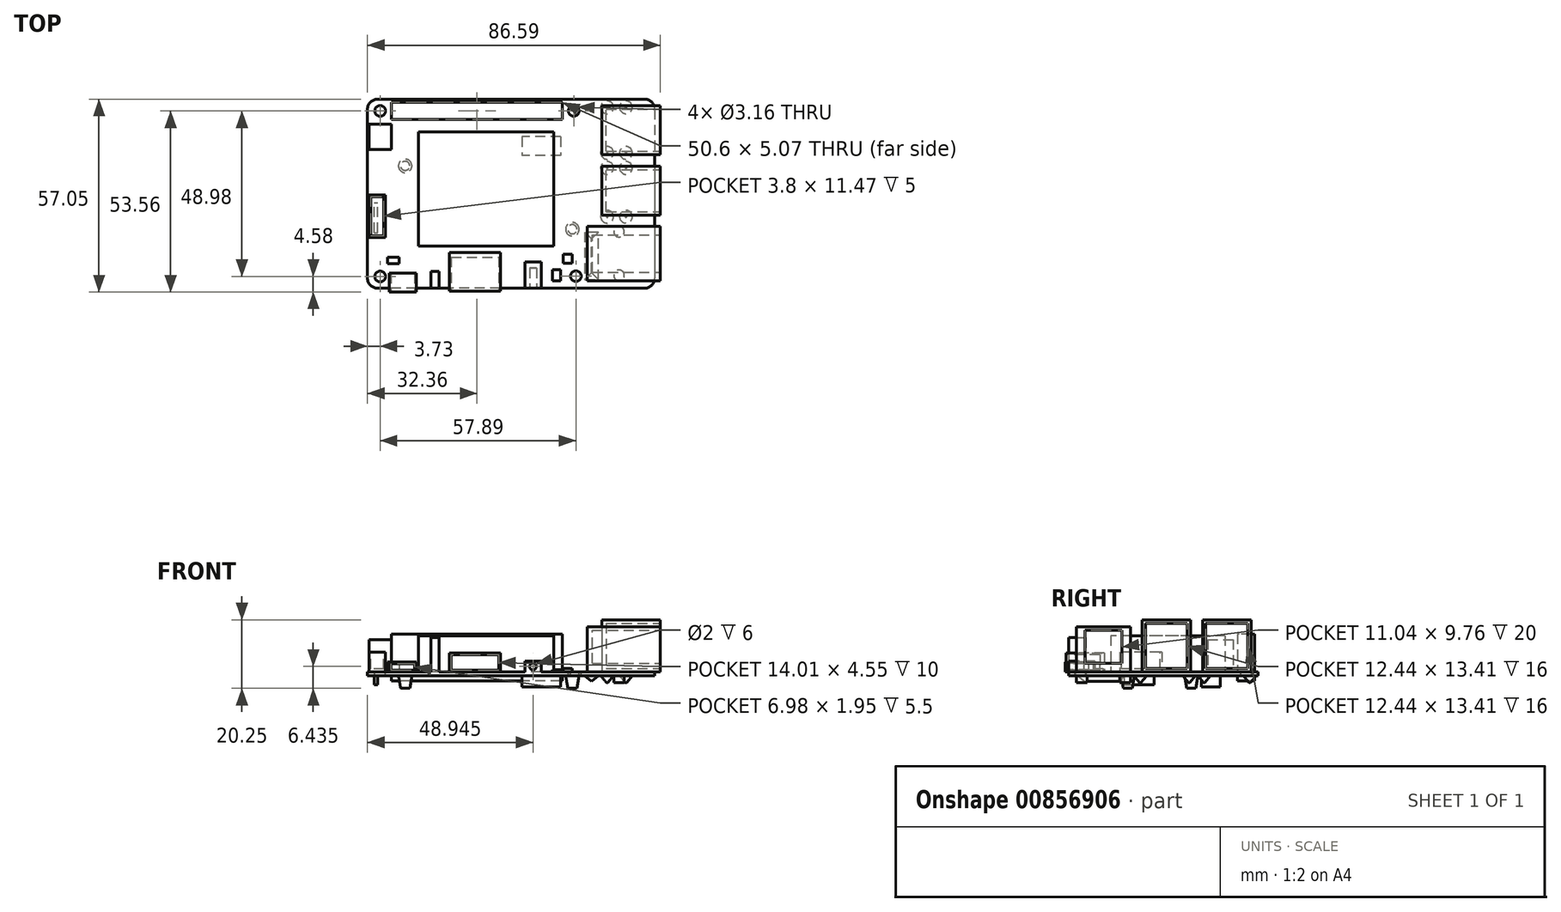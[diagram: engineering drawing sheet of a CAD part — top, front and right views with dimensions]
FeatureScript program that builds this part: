
annotation { "Feature Type Name" : "Feature", "Feature Type Description" : "" }
export const myFeature = defineFeature(function(context is Context, id is Id, definition is map)
    precondition{}
    {
        {
            var Q0;
            Q0=qCreatedBy(makeId("Top.planeOp"),FACE);
            var sketch = newSketch(context, id + "F0", { "sketchPlane" : qUnion([Q0])});
            skLineSegment(sketch, "E0.bottom", {"start": v(42.46, 27.98) * mm, "end": v(-42.46, 27.98) * mm});
            skLineSegment(sketch, "E0.top", {"start": v(42.46, -27.98) * mm, "end": v(-42.46, -27.98) * mm});
            skLineSegment(sketch, "E0.left", {"start": v(42.46, 27.98) * mm, "end": v(42.46, -27.98) * mm});
            skLineSegment(sketch, "E0.right", {"start": v(-42.46, 27.98) * mm, "end": v(-42.46, -27.98) * mm});
            skPoint(sketch, "E0.middle", {"position": v(0, 0) * mm});
            skSolve(sketch);
        }
        {
            var Q0;
            Q0=qSketchRegion(id+"F0",true);
            extrude(context, id + "F1", {"entities" : qUnion([Q0]), "depth" : 1.15 * mm, "offsetDistance" : 25 * mm});
        }
        {
            var Q0;
            Q0=makeQuery(id+"F1.opExtrude","CAP_FACE",FACE,{"disambiguationData":[OSD([sQuery(id+"F0.wireOp",EDGE,"E0.bottom"),sQuery(id+"F0.wireOp",EDGE,"E0.top"),sQuery(id+"F0.wireOp",EDGE,"E0.left"),sQuery(id+"F0.wireOp",EDGE,"E0.right")])],"isStart":false});
            var sketch = newSketch(context, id + "F2", { "sketchPlane" : qUnion([Q0])});
            skLineSegment(sketch, "E1.top", {"start": v(44.05, -9.69) * mm, "end": v(22.48, -9.69) * mm});
            skLineSegment(sketch, "E1.left", {"start": v(44.05, -25.73) * mm, "end": v(44.05, -9.69) * mm});
            skLineSegment(sketch, "E1.right", {"start": v(22.48, -25.73) * mm, "end": v(22.48, -9.69) * mm});
            skLineSegment(sketch, "E2", {"start": v(44.05, -25.73) * mm, "end": v(22.48, -25.73) * mm});
            skSolve(sketch);
        }
        {
            var Q0;
            Q0=qSketchRegion(id+"F2",true);
            extrude(context, id + "F3", {"entities" : qUnion([Q0]), "operationType" : NewBodyOperationType.ADD, "depth" : 13.33 * mm, "offsetDistance" : 25 * mm});
        }
        {
            var Q0;
            Q0=makeQuery(id+"F3.opExtrude","SWEPT_FACE",FACE,{"disambiguationData":[OSD([sQuery(id+"F2.wireOp",EDGE,"E1.left")])]});
            var sketch = newSketch(context, id + "F4", { "sketchPlane" : qUnion([Q0])});
            skLineSegment(sketch, "E3", {"start": v(-23.23, 13.45) * mm, "end": v(-12.19, 13.45) * mm});
            skLineSegment(sketch, "E4", {"start": v(-23.23, 3.7) * mm, "end": v(-23.23, 13.45) * mm});
            skLineSegment(sketch, "E5", {"start": v(-23.23, 3.7) * mm, "end": v(-12.19, 3.7) * mm});
            skLineSegment(sketch, "E6", {"start": v(-12.19, 3.7) * mm, "end": v(-12.19, 13.45) * mm});
            skSolve(sketch);
        }
        {
            var Q0;
            Q0=qSketchRegion(id+"F4",true);
            extrude(context, id + "F5", {"entities" : qUnion([Q0]), "operationType" : NewBodyOperationType.REMOVE, "oppositeDirection" : true, "depth" : 20 * mm, "offsetDistance" : 25 * mm});
        }
        {
            var Q0;
            Q0=makeQuery(id+"F1.opExtrude","CAP_FACE",FACE,{"disambiguationData":[OSD([sQuery(id+"F0.wireOp",EDGE,"E0.bottom"),sQuery(id+"F0.wireOp",EDGE,"E0.top"),sQuery(id+"F0.wireOp",EDGE,"E0.left"),sQuery(id+"F0.wireOp",EDGE,"E0.right")])],"isStart":false});
            var sketch = newSketch(context, id + "F6", { "sketchPlane" : qUnion([Q0])});
            skLineSegment(sketch, "E7", {"start": v(42.46, -25.73) * mm, "end": v(42.46, 8.12) * mm});
            skLineSegment(sketch, "E8", {"start": v(42.46, 8.12) * mm, "end": v(44.13, 8.12) * mm});
            skLineSegment(sketch, "E9.bottom", {"start": v(44.13, 8.12) * mm, "end": v(26.87, 8.12) * mm});
            skLineSegment(sketch, "E9.top", {"start": v(44.13, -6.32) * mm, "end": v(26.87, -6.32) * mm});
            skLineSegment(sketch, "E9.left", {"start": v(44.13, 8.12) * mm, "end": v(44.13, -6.32) * mm});
            skLineSegment(sketch, "E9.right", {"start": v(26.87, 8.12) * mm, "end": v(26.87, -6.32) * mm});
            skLineSegment(sketch, "E10", {"start": v(42.46, -25.73) * mm, "end": v(42.46, 26.01) * mm});
            skLineSegment(sketch, "E11", {"start": v(42.46, 26.01) * mm, "end": v(44.13, 26.01) * mm});
            skLineSegment(sketch, "E12.bottom", {"start": v(44.13, 26.01) * mm, "end": v(26.87, 26.01) * mm});
            skLineSegment(sketch, "E12.top", {"start": v(44.13, 11.57) * mm, "end": v(26.87, 11.57) * mm});
            skLineSegment(sketch, "E12.left", {"start": v(44.13, 26.01) * mm, "end": v(44.13, 11.57) * mm});
            skLineSegment(sketch, "E12.right", {"start": v(26.87, 26.01) * mm, "end": v(26.87, 11.57) * mm});
            skSolve(sketch);
        }
        {
            var Q0;
            Q0=qSketchRegion(id+"F6",true);
            extrude(context, id + "F7", {"entities" : qUnion([Q0]), "operationType" : NewBodyOperationType.ADD, "depth" : 15.4 * mm, "offsetDistance" : 25 * mm});
        }
        {
            var Q0;
            Q0=makeQuery(id+"F7.opExtrude","SWEPT_FACE",FACE,{"disambiguationData":[OSD([sQuery(id+"F6.wireOp",EDGE,"E9.left")])]});
            var sketch = newSketch(context, id + "F8", { "sketchPlane" : qUnion([Q0])});
            skLineSegment(sketch, "E13.bottom", {"start": v(-5.32, 15.56) * mm, "end": v(7.12, 15.56) * mm});
            skLineSegment(sketch, "E13.top", {"start": v(-5.32, 2.15) * mm, "end": v(7.12, 2.15) * mm});
            skLineSegment(sketch, "E13.left", {"start": v(-5.32, 15.56) * mm, "end": v(-5.32, 2.15) * mm});
            skLineSegment(sketch, "E13.right", {"start": v(7.12, 15.56) * mm, "end": v(7.12, 2.15) * mm});
            skSolve(sketch);
        }
        {
            var Q0;
            Q0=qSketchRegion(id+"F8",true);
            extrude(context, id + "F9", {"entities" : qUnion([Q0]), "operationType" : NewBodyOperationType.REMOVE, "oppositeDirection" : true, "depth" : 16 * mm, "offsetDistance" : 25 * mm});
        }
        {
            var Q0;
            Q0=makeQuery(id+"F7.opExtrude","SWEPT_FACE",FACE,{"disambiguationData":[OSD([sQuery(id+"F6.wireOp",EDGE,"E12.left")])]});
            var sketch = newSketch(context, id + "F10", { "sketchPlane" : qUnion([Q0])});
            skLineSegment(sketch, "E14.bottom", {"start": v(12.57, 15.56) * mm, "end": v(25.01, 15.56) * mm});
            skLineSegment(sketch, "E14.top", {"start": v(12.57, 2.15) * mm, "end": v(25.01, 2.15) * mm});
            skLineSegment(sketch, "E14.left", {"start": v(12.57, 15.56) * mm, "end": v(12.57, 2.15) * mm});
            skLineSegment(sketch, "E14.right", {"start": v(25.01, 15.56) * mm, "end": v(25.01, 2.15) * mm});
            skSolve(sketch);
        }
        {
            var Q0;
            Q0=qSketchRegion(id+"F10",true);
            extrude(context, id + "F11", {"entities" : qUnion([Q0]), "operationType" : NewBodyOperationType.REMOVE, "oppositeDirection" : true, "depth" : 16 * mm, "offsetDistance" : 25 * mm});
        }
        {
            var Q0;
            Q0=makeQuery(id+"F1.opExtrude","CAP_FACE",FACE,{"disambiguationData":[OSD([sQuery(id+"F0.wireOp",EDGE,"E0.bottom"),sQuery(id+"F0.wireOp",EDGE,"E0.top"),sQuery(id+"F0.wireOp",EDGE,"E0.left"),sQuery(id+"F0.wireOp",EDGE,"E0.right")])],"isStart":false});
            var sketch = newSketch(context, id + "F12", { "sketchPlane" : qUnion([Q0])});
            skLineSegment(sketch, "E15.bottom", {"start": v(15.2, 27.03) * mm, "end": v(-35.4, 27.03) * mm});
            skLineSegment(sketch, "E15.top", {"start": v(15.2, 21.96) * mm, "end": v(-35.4, 21.95) * mm});
            skLineSegment(sketch, "E15.left", {"start": v(15.2, 27.03) * mm, "end": v(15.2, 21.96) * mm});
            skLineSegment(sketch, "E15.right", {"start": v(-35.4, 27.02) * mm, "end": v(-35.4, 21.95) * mm});
            skSolve(sketch);
        }
        {
            var Q0;
            Q0=qSketchRegion(id+"F12",true);
            extrude(context, id + "F13", {"entities" : qUnion([Q0]), "operationType" : NewBodyOperationType.ADD, "depth" : 11.21 * mm, "offsetDistance" : 25 * mm, "hasSecondDirection" : true, "secondDirectionOppositeDirection" : true, "secondDirectionDepth" : 2.67 * mm});
        }
        {
            var Q0;
            Q0=makeQuery(id+"F1.opExtrude","CAP_FACE",FACE,{"disambiguationData":[OSD([sQuery(id+"F0.wireOp",EDGE,"E0.bottom"),sQuery(id+"F0.wireOp",EDGE,"E0.top"),sQuery(id+"F0.wireOp",EDGE,"E0.left"),sQuery(id+"F0.wireOp",EDGE,"E0.right")])],"isStart":false});
            var sketch = newSketch(context, id + "F14", { "sketchPlane" : qUnion([Q0])});
            skLineSegment(sketch, "E16", {"start": v(-35.4, 24.5) * mm, "end": v(-37.15, 24.5) * mm});
            skLineSegment(sketch, "E17", {"start": v(-37.15, 24.5) * mm, "end": v(-38.73, 24.5) * mm});
            skLineSegment(sketch, "E18", {"start": v(15.2, 24.5) * mm, "end": v(16.95, 24.5) * mm});
            skLineSegment(sketch, "E19", {"start": v(16.95, 24.5) * mm, "end": v(18.53, 24.5) * mm});
            skCircle(sketch, "E20", {"center": v(18.53, 24.5) * mm, "radius": 1.58 * mm});
            skLineSegment(sketch, "E21", {"start": v(-42.46, 0) * mm, "end": v(60.27, 0) * mm});
            skLineSegment(sketch, "E22", {"start": v(22.48, -25.73) * mm, "end": v(20.74, -25.73) * mm});
            skLineSegment(sketch, "E23", {"start": v(20.74, -25.73) * mm, "end": v(20.74, -18.8) * mm});
            skCircle(sketch, "E24", {"center": v(-38.73, 24.5) * mm, "radius": 1.58 * mm});
            skCircle(sketch, "E25.MirrorC", {"center": v(-38.73, -24.5) * mm, "radius": 1.58 * mm});
            skLineSegment(sketch, "E26", {"start": v(19.4, -27.98) * mm, "end": v(19.4, -25.98) * mm});
            skLineSegment(sketch, "E27", {"start": v(19.4, -24.4) * mm, "end": v(16.42, -24.4) * mm});
            skCircle(sketch, "E28", {"center": v(19.16, -24.4) * mm, "radius": 1.58 * mm});
            skSolve(sketch);
        }
        {
            var Q0;
            Q0=qSketchRegion(id+"F14",true);
            extrude(context, id + "F15", {"entities" : qUnion([Q0]), "operationType" : NewBodyOperationType.REMOVE, "endBound" : BoundingType.THROUGH_ALL, "oppositeDirection" : true, "depth" : 25 * mm, "offsetDistance" : 25 * mm});
        }
        {
            var Q0;
            Q0=makeQuery(id+"F1.opExtrude","CAP_FACE",FACE,{"disambiguationData":[OSD([sQuery(id+"F0.wireOp",EDGE,"E0.bottom"),sQuery(id+"F0.wireOp",EDGE,"E0.top"),sQuery(id+"F0.wireOp",EDGE,"E0.left"),sQuery(id+"F0.wireOp",EDGE,"E0.right")])],"isStart":false});
            var sketch = newSketch(context, id + "F16", { "sketchPlane" : qUnion([Q0])});
            skLineSegment(sketch, "E29", {"start": v(-42.46, 27.98) * mm, "end": v(-42.46, 13.12) * mm});
            skLineSegment(sketch, "E30", {"start": v(-41.96, 13.12) * mm, "end": v(-35.4, 13.12) * mm});
            skLineSegment(sketch, "E31", {"start": v(-35.4, 20.59) * mm, "end": v(-35.4, 13.12) * mm});
            skLineSegment(sketch, "E32", {"start": v(-41.96, 13.12) * mm, "end": v(-41.96, 20.59) * mm});
            skLineSegment(sketch, "E33", {"start": v(-41.96, 20.59) * mm, "end": v(-35.4, 20.59) * mm});
            skSolve(sketch);
        }
        {
            var Q0;
            Q0=qSketchRegion(id+"F16",true);
            extrude(context, id + "F17", {"entities" : qUnion([Q0]), "operationType" : NewBodyOperationType.ADD, "depth" : 9.58 * mm, "offsetDistance" : 25 * mm});
        }
        {
            var Q0;
            Q0=makeQuery(id+"F1.opExtrude","CAP_FACE",FACE,{"disambiguationData":[OSD([sQuery(id+"F0.wireOp",EDGE,"E0.bottom"),sQuery(id+"F0.wireOp",EDGE,"E0.top"),sQuery(id+"F0.wireOp",EDGE,"E0.left"),sQuery(id+"F0.wireOp",EDGE,"E0.right")])],"isStart":false});
            var sketch = newSketch(context, id + "F18", { "sketchPlane" : qUnion([Q0])});
            skLineSegment(sketch, "E34", {"start": v(-42.46, -27.98) * mm, "end": v(-42.46, -0.43) * mm});
            skLineSegment(sketch, "E35", {"start": v(-42.46, -0.43) * mm, "end": v(-41.96, -0.43) * mm});
            skLineSegment(sketch, "E36.bottom", {"start": v(-41.96, -0.43) * mm, "end": v(-37.16, -0.43) * mm});
            skLineSegment(sketch, "E36.top", {"start": v(-41.96, -12.9) * mm, "end": v(-37.16, -12.9) * mm});
            skLineSegment(sketch, "E36.left", {"start": v(-41.96, -0.43) * mm, "end": v(-41.96, -12.9) * mm});
            skLineSegment(sketch, "E36.right", {"start": v(-37.16, -0.43) * mm, "end": v(-37.16, -12.9) * mm});
            skSolve(sketch);
        }
        {
            var Q0;
            Q0=qSketchRegion(id+"F18",true);
            extrude(context, id + "F19", {"entities" : qUnion([Q0]), "operationType" : NewBodyOperationType.ADD, "depth" : 5.87 * mm, "offsetDistance" : 25 * mm});
        }
        {
            var Q0;
            Q0=makeQuery(id+"F19.opExtrude","CAP_FACE",FACE,{"disambiguationData":[OSD([sQuery(id+"F18.wireOp",EDGE,"E36.bottom"),sQuery(id+"F18.wireOp",EDGE,"E36.top"),sQuery(id+"F18.wireOp",EDGE,"E36.left"),sQuery(id+"F18.wireOp",EDGE,"E36.right")])],"isStart":false});
            var sketch = newSketch(context, id + "F20", { "sketchPlane" : qUnion([Q0])});
            skLineSegment(sketch, "E37.bottom", {"start": v(-37.16, -0.43) * mm, "end": v(-37.66, -0.43) * mm});
            skLineSegment(sketch, "E37.left", {"start": v(-37.16, -0.43) * mm, "end": v(-37.16, -0.93) * mm});
            skLineSegment(sketch, "E37.right", {"start": v(-37.66, -0.43) * mm, "end": v(-37.66, -0.93) * mm});
            skLineSegment(sketch, "E38.bottom", {"start": v(-41.96, -12.9) * mm, "end": v(-41.46, -12.9) * mm});
            skLineSegment(sketch, "E38.left", {"start": v(-41.96, -12.9) * mm, "end": v(-41.96, -12.4) * mm});
            skLineSegment(sketch, "E38.right", {"start": v(-41.46, -12.9) * mm, "end": v(-41.46, -12.4) * mm});
            skLineSegment(sketch, "E39.bottom", {"start": v(-37.66, -0.93) * mm, "end": v(-41.46, -0.93) * mm});
            skLineSegment(sketch, "E39.top", {"start": v(-37.66, -12.4) * mm, "end": v(-41.46, -12.4) * mm});
            skLineSegment(sketch, "E39.left", {"start": v(-37.66, -0.93) * mm, "end": v(-37.66, -12.4) * mm});
            skLineSegment(sketch, "E39.right", {"start": v(-41.46, -0.93) * mm, "end": v(-41.46, -12.4) * mm});
            skSolve(sketch);
        }
        {
            var Q0;
            Q0=qSketchRegion(id+"F20",true);
            extrude(context, id + "F21", {"entities" : qUnion([Q0]), "operationType" : NewBodyOperationType.REMOVE, "oppositeDirection" : true, "depth" : 5 * mm, "offsetDistance" : 25 * mm});
        }
        {
            var Q0;
            Q0=makeQuery(id+"F1.opExtrude","CAP_FACE",FACE,{"disambiguationData":[OSD([sQuery(id+"F0.wireOp",EDGE,"E0.bottom"),sQuery(id+"F0.wireOp",EDGE,"E0.top"),sQuery(id+"F0.wireOp",EDGE,"E0.left"),sQuery(id+"F0.wireOp",EDGE,"E0.right")])],"isStart":false});
            var sketch = newSketch(context, id + "F22", { "sketchPlane" : qUnion([Q0])});
            skLineSegment(sketch, "E40.0", {"start": v(44.05, -25.73) * mm, "end": v(44.05, -9.69) * mm});
            skLineSegment(sketch, "E41", {"start": v(44.05, -25.73) * mm, "end": v(8.9, -25.73) * mm});
            skLineSegment(sketch, "E42.bottom", {"start": v(4.06, -27.98) * mm, "end": v(8.9, -27.98) * mm});
            skLineSegment(sketch, "E42.top", {"start": v(4.06, -20.23) * mm, "end": v(8.9, -20.23) * mm});
            skLineSegment(sketch, "E43", {"start": v(4.06, -20.23) * mm, "end": v(4.06, -27.98) * mm});
            skLineSegment(sketch, "E44", {"start": v(8.9, -20.23) * mm, "end": v(8.9, -27.98) * mm});
            skSolve(sketch);
        }
        {
            var Q0;
            Q0=qSketchRegion(id+"F22",true);
            extrude(context, id + "F23", {"entities" : qUnion([Q0]), "operationType" : NewBodyOperationType.ADD, "depth" : 3.19 * mm, "offsetDistance" : 25 * mm});
        }
        {
            var Q0;
            Q0=makeQuery(id+"F23.boolean.opBoolean","MERGE",FACE,{"derivedFrom":[makeQuery(id+"F1.opExtrude","SWEPT_FACE",FACE,{"disambiguationData":[OSD([sQuery(id+"F0.wireOp",EDGE,"E0.top")])]}),makeQuery(id+"F23.opExtrude","SWEPT_FACE",FACE,{"disambiguationData":[OSD([sQuery(id+"F22.wireOp",EDGE,"E42.bottom")])]})]});
            var sketch = newSketch(context, id + "F24", { "sketchPlane" : qUnion([Q0])});
            skCircle(sketch, "E45", {"center": v(6.48, 2.75) * mm, "radius": 1 * mm});
            skSolve(sketch);
        }
        {
            var Q0;
            Q0=qSketchRegion(id+"F24",true);
            extrude(context, id + "F25", {"entities" : qUnion([Q0]), "operationType" : NewBodyOperationType.REMOVE, "oppositeDirection" : true, "depth" : 6 * mm, "offsetDistance" : 25 * mm});
        }
        {
            var Q0;
            Q0=makeQuery(id+"F1.opExtrude","CAP_FACE",FACE,{"disambiguationData":[OSD([sQuery(id+"F0.wireOp",EDGE,"E0.bottom"),sQuery(id+"F0.wireOp",EDGE,"E0.top"),sQuery(id+"F0.wireOp",EDGE,"E0.left"),sQuery(id+"F0.wireOp",EDGE,"E0.right")])],"isStart":false});
            var sketch = newSketch(context, id + "F26", { "sketchPlane" : qUnion([Q0])});
            skLineSegment(sketch, "E46.0", {"start": v(44.05, -25.73) * mm, "end": v(44.05, -9.69) * mm});
            skLineSegment(sketch, "E47", {"start": v(44.05, -25.73) * mm, "end": v(-21.29, -25.73) * mm});
            skLineSegment(sketch, "E48", {"start": v(-23.69, -25.73) * mm, "end": v(-23.69, -31.98) * mm});
            skLineSegment(sketch, "E49.bottom", {"start": v(-23.69, -27.98) * mm, "end": v(-21.29, -27.98) * mm});
            skLineSegment(sketch, "E49.top", {"start": v(-23.69, -22.95) * mm, "end": v(-21.29, -22.95) * mm});
            skLineSegment(sketch, "E49.left", {"start": v(-23.69, -27.98) * mm, "end": v(-23.69, -22.95) * mm});
            skLineSegment(sketch, "E49.right", {"start": v(-21.29, -27.98) * mm, "end": v(-21.29, -22.95) * mm});
            skSolve(sketch);
        }
        {
            var Q0;
            Q0=qSketchRegion(id+"F26",true);
            extrude(context, id + "F27", {"entities" : qUnion([Q0]), "operationType" : NewBodyOperationType.ADD, "depth" : 10.1 * mm, "offsetDistance" : 25 * mm});
        }
        {
            var Q0;
            Q0=makeQuery(id+"F1.opExtrude","CAP_FACE",FACE,{"disambiguationData":[OSD([sQuery(id+"F0.wireOp",EDGE,"E0.bottom"),sQuery(id+"F0.wireOp",EDGE,"E0.top"),sQuery(id+"F0.wireOp",EDGE,"E0.left"),sQuery(id+"F0.wireOp",EDGE,"E0.right")])],"isStart":false});
            var sketch = newSketch(context, id + "F28", { "sketchPlane" : qUnion([Q0])});
            skLineSegment(sketch, "E50", {"start": v(-21.29, -27.98) * mm, "end": v(-18.19, -27.98) * mm});
            skLineSegment(sketch, "E51", {"start": v(-18.19, -27.98) * mm, "end": v(-18.19, -28.78) * mm});
            skLineSegment(sketch, "E52.bottom", {"start": v(-18.19, -28.78) * mm, "end": v(-3.18, -28.78) * mm});
            skLineSegment(sketch, "E52.top", {"start": v(-18.19, -17.4) * mm, "end": v(-3.18, -17.4) * mm});
            skLineSegment(sketch, "E52.left", {"start": v(-18.19, -28.78) * mm, "end": v(-18.19, -17.4) * mm});
            skLineSegment(sketch, "E52.right", {"start": v(-3.18, -28.78) * mm, "end": v(-3.18, -17.4) * mm});
            skSolve(sketch);
        }
        {
            var Q0;
            Q0=qSketchRegion(id+"F28",true);
            extrude(context, id + "F29", {"entities" : qUnion([Q0]), "operationType" : NewBodyOperationType.ADD, "depth" : 5.55 * mm, "offsetDistance" : 25 * mm});
        }
        {
            var Q0;
            Q0=makeQuery(id+"F29.opExtrude","SWEPT_FACE",FACE,{"disambiguationData":[OSD([sQuery(id+"F28.wireOp",EDGE,"E52.bottom")])]});
            var sketch = newSketch(context, id + "F30", { "sketchPlane" : qUnion([Q0])});
            skLineSegment(sketch, "E53.bottom", {"start": v(-18.19, 6.7) * mm, "end": v(-17.69, 6.7) * mm});
            skLineSegment(sketch, "E53.left", {"start": v(-18.19, 6.7) * mm, "end": v(-18.19, 6.2) * mm});
            skLineSegment(sketch, "E53.right", {"start": v(-17.69, 6.7) * mm, "end": v(-17.69, 6.2) * mm});
            skLineSegment(sketch, "E54.bottom", {"start": v(-3.18, 1.15) * mm, "end": v(-3.68, 1.15) * mm});
            skLineSegment(sketch, "E54.left", {"start": v(-3.18, 1.15) * mm, "end": v(-3.18, 1.65) * mm});
            skLineSegment(sketch, "E54.right", {"start": v(-3.68, 1.15) * mm, "end": v(-3.68, 1.65) * mm});
            skLineSegment(sketch, "E55.bottom", {"start": v(-17.69, 6.2) * mm, "end": v(-3.68, 6.2) * mm});
            skLineSegment(sketch, "E55.top", {"start": v(-17.69, 1.65) * mm, "end": v(-3.68, 1.65) * mm});
            skLineSegment(sketch, "E55.left", {"start": v(-17.69, 6.2) * mm, "end": v(-17.69, 1.65) * mm});
            skLineSegment(sketch, "E55.right", {"start": v(-3.68, 6.2) * mm, "end": v(-3.68, 1.65) * mm});
            skSolve(sketch);
        }
        {
            var Q0;
            Q0=qSketchRegion(id+"F30",true);
            extrude(context, id + "F31", {"entities" : qUnion([Q0]), "operationType" : NewBodyOperationType.REMOVE, "oppositeDirection" : true, "depth" : 10 * mm, "offsetDistance" : 25 * mm});
        }
        {
            var Q0;
            Q0=makeQuery(id+"F1.opExtrude","CAP_FACE",FACE,{"disambiguationData":[OSD([sQuery(id+"F0.wireOp",EDGE,"E0.bottom"),sQuery(id+"F0.wireOp",EDGE,"E0.top"),sQuery(id+"F0.wireOp",EDGE,"E0.left"),sQuery(id+"F0.wireOp",EDGE,"E0.right")])],"isStart":false});
            var sketch = newSketch(context, id + "F32", { "sketchPlane" : qUnion([Q0])});
            skLineSegment(sketch, "E56", {"start": v(-42.46, -27.98) * mm, "end": v(-35.98, -27.98) * mm});
            skLineSegment(sketch, "E57", {"start": v(-28, -27.98) * mm, "end": v(-28, -29.07) * mm});
            skLineSegment(sketch, "E58.bottom", {"start": v(-28, -29.07) * mm, "end": v(-35.98, -29.07) * mm});
            skLineSegment(sketch, "E58.top", {"start": v(-28, -23.52) * mm, "end": v(-35.98, -23.52) * mm});
            skLineSegment(sketch, "E58.left", {"start": v(-28, -29.07) * mm, "end": v(-28, -23.52) * mm});
            skLineSegment(sketch, "E58.right", {"start": v(-35.98, -29.08) * mm, "end": v(-35.98, -23.52) * mm});
            skSolve(sketch);
        }
        {
            var Q0;
            Q0=qSketchRegion(id+"F32",true);
            extrude(context, id + "F33", {"entities" : qUnion([Q0]), "operationType" : NewBodyOperationType.ADD, "depth" : 2.95 * mm, "offsetDistance" : 25 * mm});
        }
        {
            var Q0;
            Q0=makeQuery(id+"F1.opExtrude","CAP_FACE",FACE,{"disambiguationData":[OSD([sQuery(id+"F0.wireOp",EDGE,"E0.bottom"),sQuery(id+"F0.wireOp",EDGE,"E0.top"),sQuery(id+"F0.wireOp",EDGE,"E0.left"),sQuery(id+"F0.wireOp",EDGE,"E0.right")])],"isStart":false});
            var sketch = newSketch(context, id + "F34", { "sketchPlane" : qUnion([Q0])});
            skLineSegment(sketch, "E59", {"start": v(-35.98, -23.52) * mm, "end": v(-35.98, -20.7) * mm});
            skLineSegment(sketch, "E60", {"start": v(-35.98, -20.7) * mm, "end": v(-36.48, -20.7) * mm});
            skLineSegment(sketch, "E61.bottom", {"start": v(-36.48, -20.7) * mm, "end": v(-33.11, -20.7) * mm});
            skLineSegment(sketch, "E61.top", {"start": v(-36.48, -18.8) * mm, "end": v(-33.11, -18.8) * mm});
            skLineSegment(sketch, "E61.left", {"start": v(-36.48, -20.7) * mm, "end": v(-36.48, -18.8) * mm});
            skLineSegment(sketch, "E61.right", {"start": v(-33.11, -20.7) * mm, "end": v(-33.11, -18.8) * mm});
            skSolve(sketch);
        }
        {
            var Q0;
            Q0=qSketchRegion(id+"F34",true);
            extrude(context, id + "F35", {"entities" : qUnion([Q0]), "operationType" : NewBodyOperationType.ADD, "depth" : 2.96 * mm, "offsetDistance" : 25 * mm});
        }
        {
            var Q0;
            Q0=makeQuery(id+"F33.opExtrude","SWEPT_FACE",FACE,{"disambiguationData":[OSD([sQuery(id+"F32.wireOp",EDGE,"E58.bottom")])]});
            var sketch = newSketch(context, id + "F36", { "sketchPlane" : qUnion([Q0])});
            skLineSegment(sketch, "E62.bottom", {"start": v(-35.48, 3.6) * mm, "end": v(-28.5, 3.6) * mm});
            skLineSegment(sketch, "E62.top", {"start": v(-35.48, 1.65) * mm, "end": v(-28.5, 1.65) * mm});
            skLineSegment(sketch, "E62.left", {"start": v(-35.48, 3.6) * mm, "end": v(-35.48, 1.65) * mm});
            skLineSegment(sketch, "E62.right", {"start": v(-28.5, 3.6) * mm, "end": v(-28.5, 1.65) * mm});
            skSolve(sketch);
        }
        {
            var Q0;
            Q0=qSketchRegion(id+"F36",true);
            extrude(context, id + "F37", {"entities" : qUnion([Q0]), "operationType" : NewBodyOperationType.REMOVE, "oppositeDirection" : true, "depth" : 5.5 * mm, "offsetDistance" : 25 * mm});
        }
        {
            var Q0;
            Q0=makeQuery(id+"F1.opExtrude","CAP_FACE",FACE,{"disambiguationData":[OSD([sQuery(id+"F0.wireOp",EDGE,"E0.bottom"),sQuery(id+"F0.wireOp",EDGE,"E0.top"),sQuery(id+"F0.wireOp",EDGE,"E0.left"),sQuery(id+"F0.wireOp",EDGE,"E0.right")])],"isStart":false});
            var sketch = newSketch(context, id + "F38", { "sketchPlane" : qUnion([Q0])});
            skLineSegment(sketch, "E63", {"start": v(19.4, -25.73) * mm, "end": v(18.06, -25.73) * mm});
            skLineSegment(sketch, "E64", {"start": v(18.06, -25.73) * mm, "end": v(14.65, -25.73) * mm});
            skLineSegment(sketch, "E65.bottom", {"start": v(14.65, -25.73) * mm, "end": v(12.19, -25.73) * mm});
            skLineSegment(sketch, "E65.top", {"start": v(14.65, -22.53) * mm, "end": v(12.19, -22.53) * mm});
            skLineSegment(sketch, "E65.left", {"start": v(14.65, -25.73) * mm, "end": v(14.65, -22.53) * mm});
            skLineSegment(sketch, "E65.right", {"start": v(12.19, -25.73) * mm, "end": v(12.19, -22.53) * mm});
            skSolve(sketch);
        }
        {
            var Q0;
            Q0=qSketchRegion(id+"F38",true);
            extrude(context, id + "F39", {"entities" : qUnion([Q0]), "operationType" : NewBodyOperationType.ADD, "depth" : 0.6 * mm, "offsetDistance" : 25 * mm});
        }
        {
            var Q0;
            Q0=makeQuery(id+"F1.opExtrude","CAP_FACE",FACE,{"disambiguationData":[OSD([sQuery(id+"F0.wireOp",EDGE,"E0.bottom"),sQuery(id+"F0.wireOp",EDGE,"E0.top"),sQuery(id+"F0.wireOp",EDGE,"E0.left"),sQuery(id+"F0.wireOp",EDGE,"E0.right")])],"isStart":false});
            var sketch = newSketch(context, id + "F40", { "sketchPlane" : qUnion([Q0])});
            skLineSegment(sketch, "E66", {"start": v(14.65, -22.53) * mm, "end": v(14.65, -20.53) * mm});
            skLineSegment(sketch, "E67", {"start": v(19.4, -25.73) * mm, "end": v(18.06, -25.73) * mm});
            skLineSegment(sketch, "E68.bottom", {"start": v(18.06, -20.53) * mm, "end": v(15.43, -20.53) * mm});
            skLineSegment(sketch, "E68.top", {"start": v(18.06, -17.9) * mm, "end": v(15.43, -17.9) * mm});
            skLineSegment(sketch, "E68.left", {"start": v(18.06, -20.53) * mm, "end": v(18.06, -17.9) * mm});
            skLineSegment(sketch, "E68.right", {"start": v(15.43, -20.53) * mm, "end": v(15.43, -17.9) * mm});
            skSolve(sketch);
        }
        {
            var Q0;
            Q0=qSketchRegion(id+"F40",true);
            extrude(context, id + "F41", {"entities" : qUnion([Q0]), "operationType" : NewBodyOperationType.ADD, "depth" : 1 * mm, "offsetDistance" : 25 * mm});
        }
        {
            var Q0;
            Q0=makeQuery(id+"F1.opExtrude","CAP_FACE",FACE,{"disambiguationData":[OSD([sQuery(id+"F0.wireOp",EDGE,"E0.bottom"),sQuery(id+"F0.wireOp",EDGE,"E0.top"),sQuery(id+"F0.wireOp",EDGE,"E0.left"),sQuery(id+"F0.wireOp",EDGE,"E0.right")])],"isStart":false});
            var sketch = newSketch(context, id + "F42", { "sketchPlane" : qUnion([Q0])});
            skLineSegment(sketch, "E69", {"start": v(15.2, 21.96) * mm, "end": v(15.2, 18.27) * mm});
            skLineSegment(sketch, "E70.0", {"start": v(-35.4, 27.03) * mm, "end": v(-35.4, 21.95) * mm});
            skLineSegment(sketch, "E71.0", {"start": v(15.2, 27.03) * mm, "end": v(15.2, 21.96) * mm});
            skLineSegment(sketch, "E72", {"start": v(15.2, 18.27) * mm, "end": v(12.67, 18.27) * mm});
            skLineSegment(sketch, "E73.bottom", {"start": v(12.67, 18.27) * mm, "end": v(-27.34, 18.27) * mm});
            skLineSegment(sketch, "E73.top", {"start": v(12.67, -15.54) * mm, "end": v(-27.34, -15.54) * mm});
            skLineSegment(sketch, "E73.left", {"start": v(12.67, 18.27) * mm, "end": v(12.67, -15.54) * mm});
            skLineSegment(sketch, "E73.right", {"start": v(-27.34, 18.27) * mm, "end": v(-27.34, -15.54) * mm});
            skSolve(sketch);
        }
        {
            var Q0;
            Q0=qSketchRegion(id+"F42",true);
            extrude(context, id + "F43", {"entities" : qUnion([Q0]), "operationType" : NewBodyOperationType.ADD, "depth" : 10.71 * mm, "offsetDistance" : 25 * mm});
        }
        {
            var Q0;
            Q0=makeQuery(id+"F1.opExtrude","CAP_FACE",FACE,{"disambiguationData":[OSD([sQuery(id+"F0.wireOp",EDGE,"E0.bottom"),sQuery(id+"F0.wireOp",EDGE,"E0.top"),sQuery(id+"F0.wireOp",EDGE,"E0.left"),sQuery(id+"F0.wireOp",EDGE,"E0.right")])],"isStart":true});
            var sketch = newSketch(context, id + "F44", { "sketchPlane" : qUnion([Q0])});
            skLineSegment(sketch, "E74.bottom", {"start": v(-40.46, 11.5) * mm, "end": v(-39.46, 11.5) * mm});
            skLineSegment(sketch, "E74.top", {"start": v(-40.46, 2.73) * mm, "end": v(-39.46, 2.73) * mm});
            skLineSegment(sketch, "E74.right", {"start": v(-39.46, 11.5) * mm, "end": v(-39.46, 2.73) * mm});
            skLineSegment(sketch, "E75", {"start": v(-40.46, 11.5) * mm, "end": v(-40.46, 2.73) * mm});
            skSolve(sketch);
        }
        {
            var Q0;
            Q0=qSketchRegion(id+"F44",true);
            extrude(context, id + "F45", {"entities" : qUnion([Q0]), "operationType" : NewBodyOperationType.ADD, "depth" : 2.67 * mm, "offsetDistance" : 25 * mm});
        }
        {
            var Q0;
            Q0=makeQuery(id+"F1.opExtrude","CAP_FACE",FACE,{"disambiguationData":[OSD([sQuery(id+"F0.wireOp",EDGE,"E0.bottom"),sQuery(id+"F0.wireOp",EDGE,"E0.top"),sQuery(id+"F0.wireOp",EDGE,"E0.left"),sQuery(id+"F0.wireOp",EDGE,"E0.right")])],"isStart":true});
            var sketch = newSketch(context, id + "F46", { "sketchPlane" : qUnion([Q0])});
            skCircle(sketch, "E76", {"center": v(33.97, -25.56) * mm, "radius": 1.89 * mm});
            skCircle(sketch, "E77.MirrorC", {"center": v(28.4, -25.56) * mm, "radius": 1.89 * mm});
            skPoint(sketch, "E78.0.end.orphan", {"position": v(42.46, -11.57) * mm});
            skPoint(sketch, "E78.0.start.orphan", {"position": v(44.13, -11.57) * mm});
            skLineSegment(sketch, "E79.0", {"start": v(44.13, -8.12) * mm, "end": v(42.46, -8.12) * mm});
            skLineSegment(sketch, "E80.0", {"start": v(44.13, 6.32) * mm, "end": v(42.46, 6.32) * mm});
            skLineSegment(sketch, "E81.0", {"start": v(44.13, -11.57) * mm, "end": v(42.46, -11.57) * mm});
            skCircle(sketch, "E82", {"center": v(33.97, -12.07) * mm, "radius": 1.89 * mm});
            skCircle(sketch, "E83", {"center": v(28.4, -12.07) * mm, "radius": 1.89 * mm});
            skCircle(sketch, "E84", {"center": v(33.97, -7.62) * mm, "radius": 1.89 * mm});
            skCircle(sketch, "E85", {"center": v(28.4, -7.62) * mm, "radius": 1.89 * mm});
            skCircle(sketch, "E86", {"center": v(33.97, 6.82) * mm, "radius": 1.89 * mm});
            skCircle(sketch, "E87", {"center": v(28.4, 6.82) * mm, "radius": 1.89 * mm});
            skSolve(sketch);
        }
        {
            var Q0;
            Q0=qSketchRegion(id+"F46",true);
            extrude(context, id + "F47", {"entities" : qUnion([Q0]), "operationType" : NewBodyOperationType.ADD, "depth" : 2 * mm, "offsetDistance" : 25 * mm, "hasDraft" : true, "draftAngle" : 40 * degree, "draftPullDirection" : true});
        }
        {
            var Q0;
            Q0=makeQuery(id+"F1.opExtrude","CAP_FACE",FACE,{"disambiguationData":[OSD([sQuery(id+"F0.wireOp",EDGE,"E0.bottom"),sQuery(id+"F0.wireOp",EDGE,"E0.top"),sQuery(id+"F0.wireOp",EDGE,"E0.left"),sQuery(id+"F0.wireOp",EDGE,"E0.right")])],"isStart":true});
            var sketch = newSketch(context, id + "F48", { "sketchPlane" : qUnion([Q0])});
            skLineSegment(sketch, "E88.bottom", {"start": v(14.7, -16.86) * mm, "end": v(3.15, -16.86) * mm});
            skLineSegment(sketch, "E88.top", {"start": v(14.7, -11.3) * mm, "end": v(3.15, -11.3) * mm});
            skLineSegment(sketch, "E88.left", {"start": v(14.7, -16.86) * mm, "end": v(14.7, -11.3) * mm});
            skLineSegment(sketch, "E88.right", {"start": v(3.15, -16.86) * mm, "end": v(3.15, -11.3) * mm});
            skSolve(sketch);
        }
        {
            var Q0;
            Q0=qSketchRegion(id+"F48",true);
            extrude(context, id + "F49", {"entities" : qUnion([Q0]), "operationType" : NewBodyOperationType.ADD, "depth" : 3.24 * mm, "offsetDistance" : 25 * mm});
        }
        {
            var Q0;
            Q0=makeQuery(id+"F1.opExtrude","CAP_FACE",FACE,{"disambiguationData":[OSD([sQuery(id+"F0.wireOp",EDGE,"E0.bottom"),sQuery(id+"F0.wireOp",EDGE,"E0.top"),sQuery(id+"F0.wireOp",EDGE,"E0.left"),sQuery(id+"F0.wireOp",EDGE,"E0.right")])],"isStart":true});
            var sketch = newSketch(context, id + "F50", { "sketchPlane" : qUnion([Q0])});
            skLineSegment(sketch, "E89", {"start": v(42.46, 25.73) * mm, "end": v(31.92, 25.73) * mm});
            skLineSegment(sketch, "E90", {"start": v(31.92, 25.73) * mm, "end": v(31.92, 24.16) * mm});
            skCircle(sketch, "E91", {"center": v(31.92, 24.16) * mm, "radius": 1.57 * mm});
            skLineSegment(sketch, "E92", {"start": v(31.92, 9.69) * mm, "end": v(31.92, 11.26) * mm});
            skCircle(sketch, "E93", {"center": v(31.92, 11.26) * mm, "radius": 1.57 * mm});
            skSolve(sketch);
        }
        {
            var Q0;
            Q0=qSketchRegion(id+"F50",true);
            extrude(context, id + "F51", {"entities" : qUnion([Q0]), "operationType" : NewBodyOperationType.ADD, "depth" : 2.06 * mm, "offsetDistance" : 25 * mm});
        }
        {
            var Q0;
            Q0=makeQuery(id+"F1.opExtrude","CAP_FACE",FACE,{"disambiguationData":[OSD([sQuery(id+"F0.wireOp",EDGE,"E0.bottom"),sQuery(id+"F0.wireOp",EDGE,"E0.top"),sQuery(id+"F0.wireOp",EDGE,"E0.left"),sQuery(id+"F0.wireOp",EDGE,"E0.right")])],"isStart":true});
            var sketch = newSketch(context, id + "F52", { "sketchPlane" : qUnion([Q0])});
            skLineSegment(sketch, "E94", {"start": v(25.84, 11.38) * mm, "end": v(29.02, 11.38) * mm});
            skPoint(sketch, "E95", {"position": v(25.84, 11.38) * mm});
            skLineSegment(sketch, "E96.bottom", {"start": v(25.84, 11.38) * mm, "end": v(21.8, 11.38) * mm});
            skLineSegment(sketch, "E96.top", {"start": v(25.84, 25.41) * mm, "end": v(21.8, 25.41) * mm});
            skLineSegment(sketch, "E96.left", {"start": v(25.84, 11.38) * mm, "end": v(25.84, 25.41) * mm});
            skLineSegment(sketch, "E96.right", {"start": v(21.8, 11.38) * mm, "end": v(21.8, 25.41) * mm});
            skSolve(sketch);
        }
        {
            var Q0;
            Q0=qSketchRegion(id+"F52",true);
            extrude(context, id + "F53", {"entities" : qUnion([Q0]), "operationType" : NewBodyOperationType.ADD, "depth" : 1.76 * mm, "offsetDistance" : 25 * mm, "hasDraft" : true, "draftAngle" : 50 * degree, "draftPullDirection" : true});
        }
        {
            var Q0;
            Q0=makeQuery(id+"F1.opExtrude","CAP_FACE",FACE,{"disambiguationData":[OSD([sQuery(id+"F0.wireOp",EDGE,"E0.bottom"),sQuery(id+"F0.wireOp",EDGE,"E0.top"),sQuery(id+"F0.wireOp",EDGE,"E0.left"),sQuery(id+"F0.wireOp",EDGE,"E0.right")])],"isStart":true});
            var sketch = newSketch(context, id + "F54", { "sketchPlane" : qUnion([Q0])});
            skLineSegment(sketch, "E97.bottom", {"start": v(-42.46, -27.98) * mm, "end": v(-31.32, -27.98) * mm});
            skLineSegment(sketch, "E97.left", {"start": v(-42.46, -27.98) * mm, "end": v(-42.46, -8.24) * mm});
            skCircle(sketch, "E98", {"center": v(-31.32, -8.24) * mm, "radius": 2 * mm});
            skLineSegment(sketch, "E99.bottom", {"start": v(42.46, 27.98) * mm, "end": v(16.14, 27.98) * mm});
            skLineSegment(sketch, "E99.left", {"start": v(42.46, 27.98) * mm, "end": v(42.46, 8.53) * mm});
            skCircle(sketch, "E100", {"center": v(18.13, 10.52) * mm, "radius": 2 * mm});
            skSolve(sketch);
        }
        {
            var Q0;
            Q0=qSketchRegion(id+"F54",true);
            extrude(context, id + "F55", {"entities" : qUnion([Q0]), "operationType" : NewBodyOperationType.ADD, "depth" : 3.69 * mm, "offsetDistance" : 25 * mm, "hasDraft" : true, "draftAngle" : 10 * degree, "draftPullDirection" : true});
        }
        {
            var Q0;
            Q0=makeQuery(id+"F1.opExtrude","SWEPT_EDGE",EDGE,{"disambiguationData":[OSD([sQuery(id+"F0.wireOp",EDGE,"E0.top"),sQuery(id+"F0.wireOp",EDGE,"E0.right")])]});
            var Q1;
            Q1=makeQuery(id+"F1.opExtrude","SWEPT_EDGE",EDGE,{"disambiguationData":[OSD([sQuery(id+"F0.wireOp",EDGE,"E0.top"),sQuery(id+"F0.wireOp",EDGE,"E0.left")])]});
            var Q2;
            Q2=makeQuery(id+"F1.opExtrude","SWEPT_EDGE",EDGE,{"disambiguationData":[OSD([sQuery(id+"F0.wireOp",EDGE,"E0.bottom"),sQuery(id+"F0.wireOp",EDGE,"E0.left")])]});
            var Q3;
            Q3=makeQuery(id+"F1.opExtrude","SWEPT_EDGE",EDGE,{"disambiguationData":[OSD([sQuery(id+"F0.wireOp",EDGE,"E0.bottom"),sQuery(id+"F0.wireOp",EDGE,"E0.right")])]});
            fillet(context, id + "F56", {"entities" : qUnion([Q0, Q1, Q2, Q3]), "radius" : 3 * mm, "tangentPropagation" : true, "allowEdgeOverflow" : false});
        }
    });
